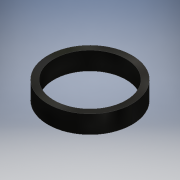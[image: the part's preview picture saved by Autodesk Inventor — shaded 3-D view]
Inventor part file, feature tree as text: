
AUTODESK INVENTOR PART (.ipt)
format: ipt  version: 2016 (Build 200138000, 138)  size: 99,840 bytes
history: native  units: mm
features: other x1, extrude x1, sketch x1
ambient origin geometry x8: Origin, YZ Plane, XZ Plane, XY Plane, X Axis, Y Axis, Z Axis, Center Point
bodies: Body1 (feature_tree)
feature tree (3):
  other  "ソリッド1"
  extrude  "押し出し1"  Depth=12.0mm
  sketch  "スケッチ1"
